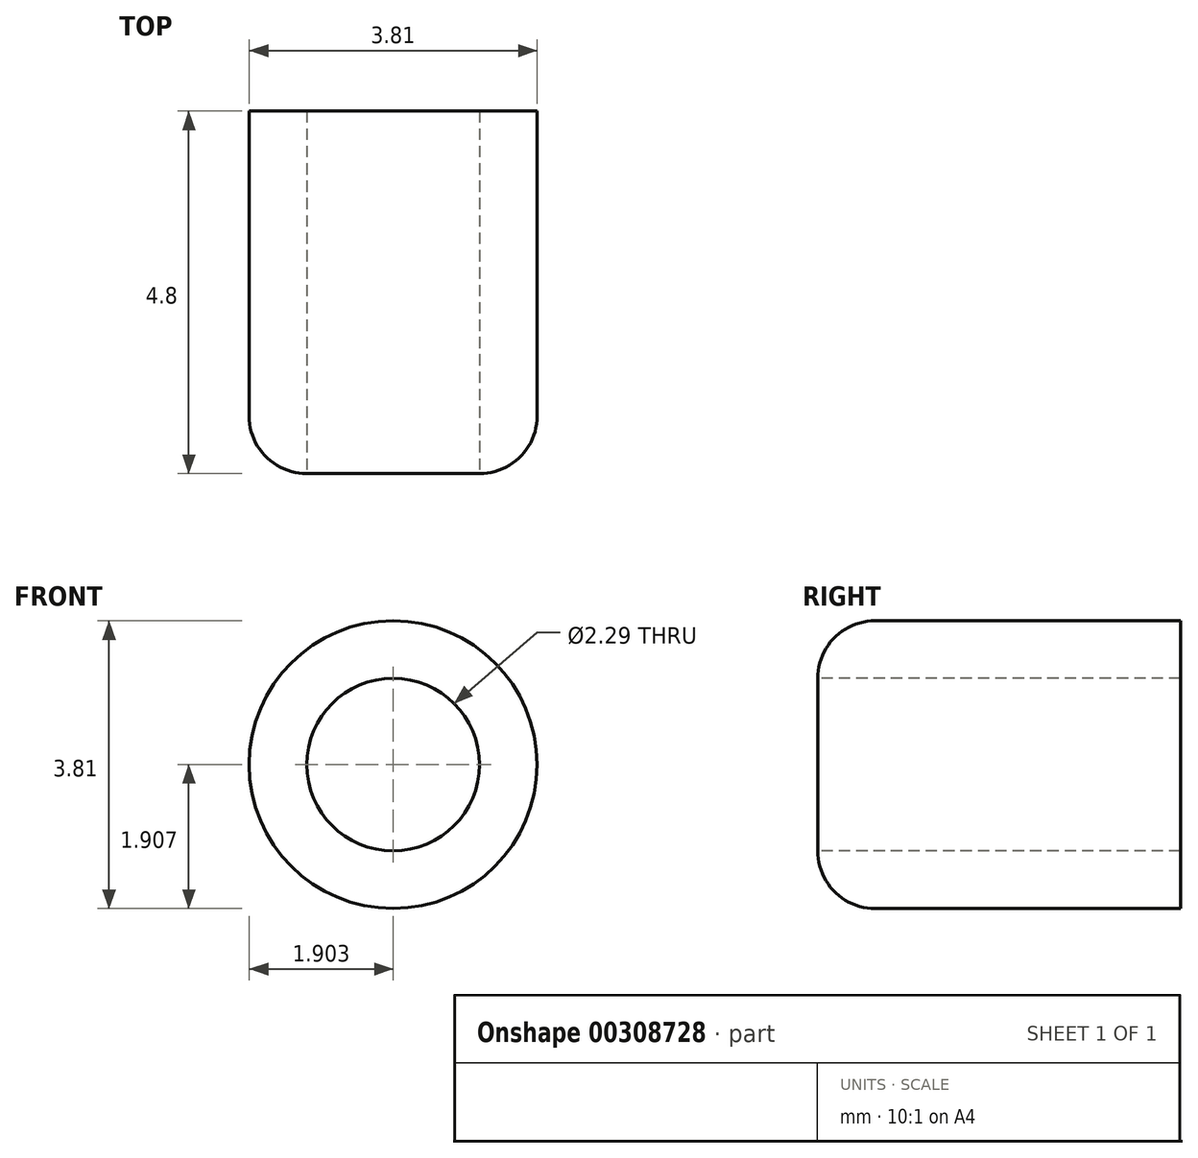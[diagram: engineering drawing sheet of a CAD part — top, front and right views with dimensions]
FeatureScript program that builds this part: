
annotation { "Feature Type Name" : "Feature", "Feature Type Description" : "" }
export const myFeature = defineFeature(function(context is Context, id is Id, definition is map)
    precondition{}
    {
        {
            var Q0;
            Q0=qCreatedBy(makeId("Front.planeOp"),FACE);
            var sketch = newSketch(context, id + "F0", { "sketchPlane" : qUnion([Q0])});
            skCircle(sketch, "E0", {"center": v(-14.55, 10.38) * mm, "radius": 1.9 * mm});
            skSolve(sketch);
        }
        {
            var Q0;
            Q0=makeQuery(id+"F0.imprint","IMPRINT",FACE,{"disambiguationData":[TD([[makeQuery(id+"F0.imprint","IMPRINT",EDGE,{"derivedFrom":sQuery(id+"F0.wireOp",EDGE,"E0")}),1.0]])]});
            extrude(context, id + "F1", {"entities" : qUnion([Q0]), "oppositeDirection" : true, "depth" : 4.8 * mm});
        }
        {
            var Q0;
            Q0=makeQuery(id+"F1.opExtrude","CAP_EDGE",EDGE,{"disambiguationData":[OSD([sQuery(id+"F0.wireOp",EDGE,"E0")])],"isStart":true});
            fillet(context, id + "F2", {"entities" : qUnion([Q0]), "radius" : 0.76 * mm, "tangentPropagation" : true, "allowEdgeOverflow" : false});
        }
        {
            var Q0;
            Q0=makeQuery(id+"F1.opExtrude","CAP_FACE",FACE,{"disambiguationData":[OSD([sQuery(id+"F0.wireOp",EDGE,"E0")])],"isStart":true});
            var sketch = newSketch(context, id + "F3", { "sketchPlane" : qUnion([Q0])});
            skPoint(sketch, "E1", {"position": v(-14.55, 10.38) * mm});
            skSolve(sketch);
        }
        {
            var Q0;
            Q0=sQuery(id+"F3.wireOp",VERTEX,"E1");
            var Q1;
            Q1=makeQuery(id+"F1.opExtrude","SWEPT_BODY",BODY,{"disambiguationData":[OSD([sQuery(id+"F0.wireOp",EDGE,"E0")])]});
            hole(context, id + "F4", {"style" : HoleStyle.SIMPLE, "endStyle" : HoleEndStyle.THROUGH, "holeDiameter" : 2.3 * mm, "tappedDepth" : 12.7 * mm, "tapClearance" : 3, "locations" : qUnion([Q0]), "scope" : qUnion([Q1])});
        }
    });
